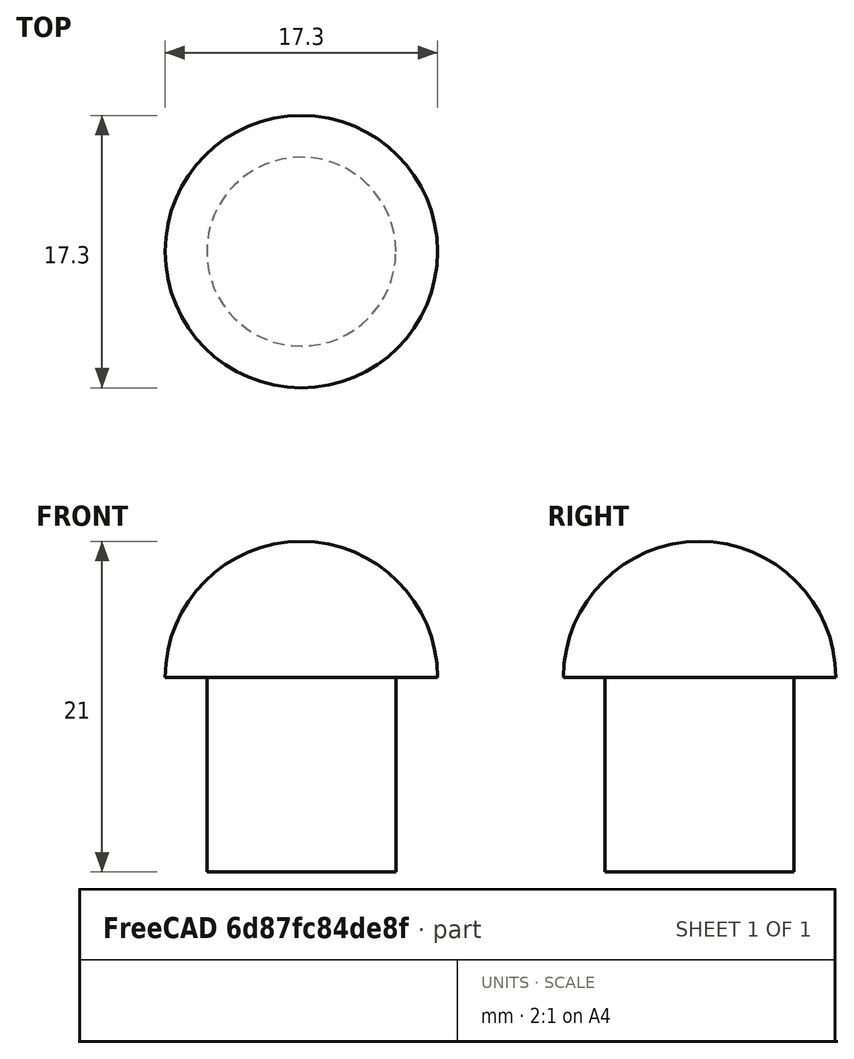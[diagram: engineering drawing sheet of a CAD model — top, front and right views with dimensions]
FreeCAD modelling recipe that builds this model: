
FCSTD DOCUMENT  (FreeCAD 0.19R)
Label: CLDIY Wasserdichte Momentary Push Button
License: All rights reserved
LicenseURL: http://en.wikipedia.org/wiki/All_rights_reserved
objects: Sketcher::SketchObject×1, PartDesign::Revolution×1, PartDesign::Body×1
note: 4 computed .brp shape members not serialized (recipe doc carries the construction recipe); baked Part::Feature solids carry a one-line shape summary decoded from their .brp

FEATURE [Sketcher::SketchObject] Sketch
  FullyConstrained = true
  MapMode = 5
  Placement = pos=(0,0,0) rot=(0.57735,0.57735,0.57735;2.0944rad)
  Support = -> [YZ_Plane]
  sketch-geometry (5):
    g0: LineSegment StartX=8.65 StartY=0 StartZ=0 EndX=6 EndY=0 EndZ=0
    g1: LineSegment StartX=6 StartY=0 StartZ=0 EndX=6 EndY=-12.35 EndZ=0
    g2: LineSegment StartX=6 StartY=-12.35 StartZ=0 EndX=0 EndY=-12.35 EndZ=0
    g3: LineSegment StartX=0 StartY=-12.35 StartZ=0 EndX=5e-16 EndY=8.65 EndZ=0
    g4: ArcOfCircle CenterX=0 CenterY=0 CenterZ=0 NormalX=0 NormalY=0 NormalZ=1 AngleXU=0 Radius=8.65 StartAngle=0 EndAngle=1.5708
  constraints (15):
    c: PointOnObject(g0,g-1)
    c: Coincident(g0,g1)
    c: Vertical(g1)
    c: Coincident(g1,g2)
    c: PointOnObject(g2,g-2)
    c: Horizontal(g2)
    c: Coincident(g2,g3)
    c: DistanceX(g-1,g0) = 6
    c: DistanceY(g2,g-1) = 12.35
    c: Coincident(g4,g-1)
    c: Coincident(g4,g0)
    c: PointOnObject(g4,g-2)
    c: Radius(g4) = 8.65
    c: Horizontal(g4,g0)
    c: Coincident(g3,g4)
FEATURE [PartDesign::Revolution] Revolution
  Angle = 360
  Axis = (-2e-16,3e-16,1)
  Base = (0,0,0)
  Placement = pos=(0,0,0) rot=(0.57735,0.57735,0.57735;2.0944rad)
  Profile = -> Sketch
  ReferenceAxis = -> Sketch [V_Axis]
  Reversed = true
FEATURE [PartDesign::Body] Body
  Group = -> [Sketch,Revolution]
  Origin = -> Origin
  Tip = -> Revolution
